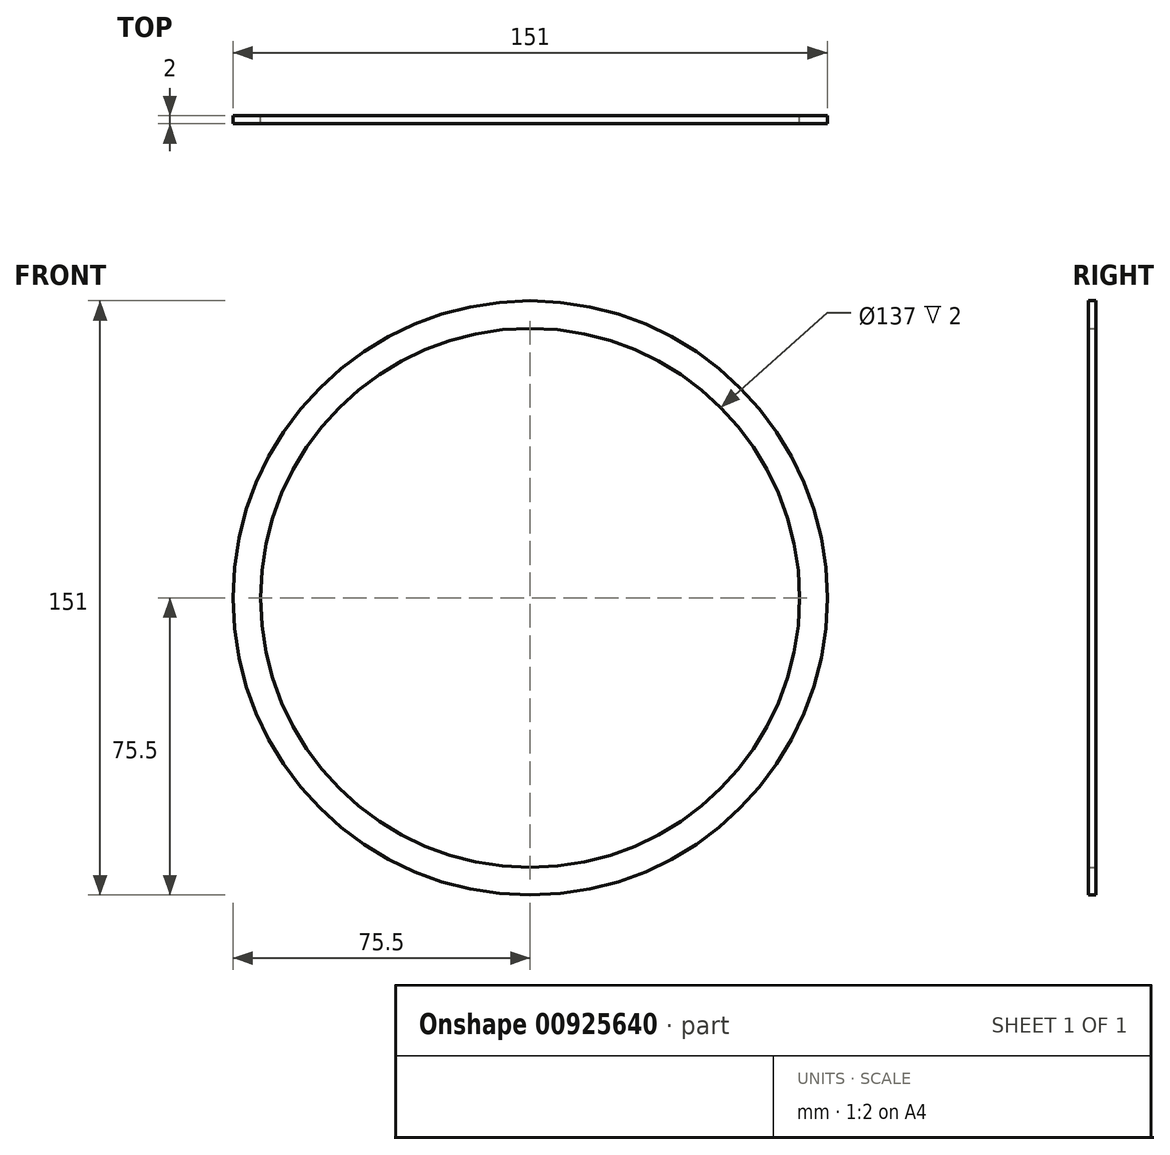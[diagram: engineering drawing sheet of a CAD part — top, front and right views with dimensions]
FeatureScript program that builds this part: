
annotation { "Feature Type Name" : "Feature", "Feature Type Description" : "" }
export const myFeature = defineFeature(function(context is Context, id is Id, definition is map)
    precondition{}
    {
        {
            var Q0;
            Q0=qCreatedBy(makeId("Front.planeOp"),FACE);
            var sketch = newSketch(context, id + "F0", { "sketchPlane" : qUnion([Q0])});
            skCircle(sketch, "E0", {"center": v(0, 0) * mm, "radius": 75.5 * mm});
            skCircle(sketch, "E1", {"center": v(0, 0) * mm, "radius": 68.5 * mm});
            skSolve(sketch);
        }
        {
            var Q0;
            Q0=makeQuery(id+"F0.imprint","IMPRINT",FACE,{"disambiguationData":[TD([[makeQuery(id+"F0.imprint","IMPRINT",EDGE,{"derivedFrom":sQuery(id+"F0.wireOp",EDGE,"E0")}),1.0]])]});
            extrude(context, id + "F1", {"entities" : qUnion([Q0]), "depth" : 2 * mm, "offsetDistance" : 25 * mm});
        }
    });
